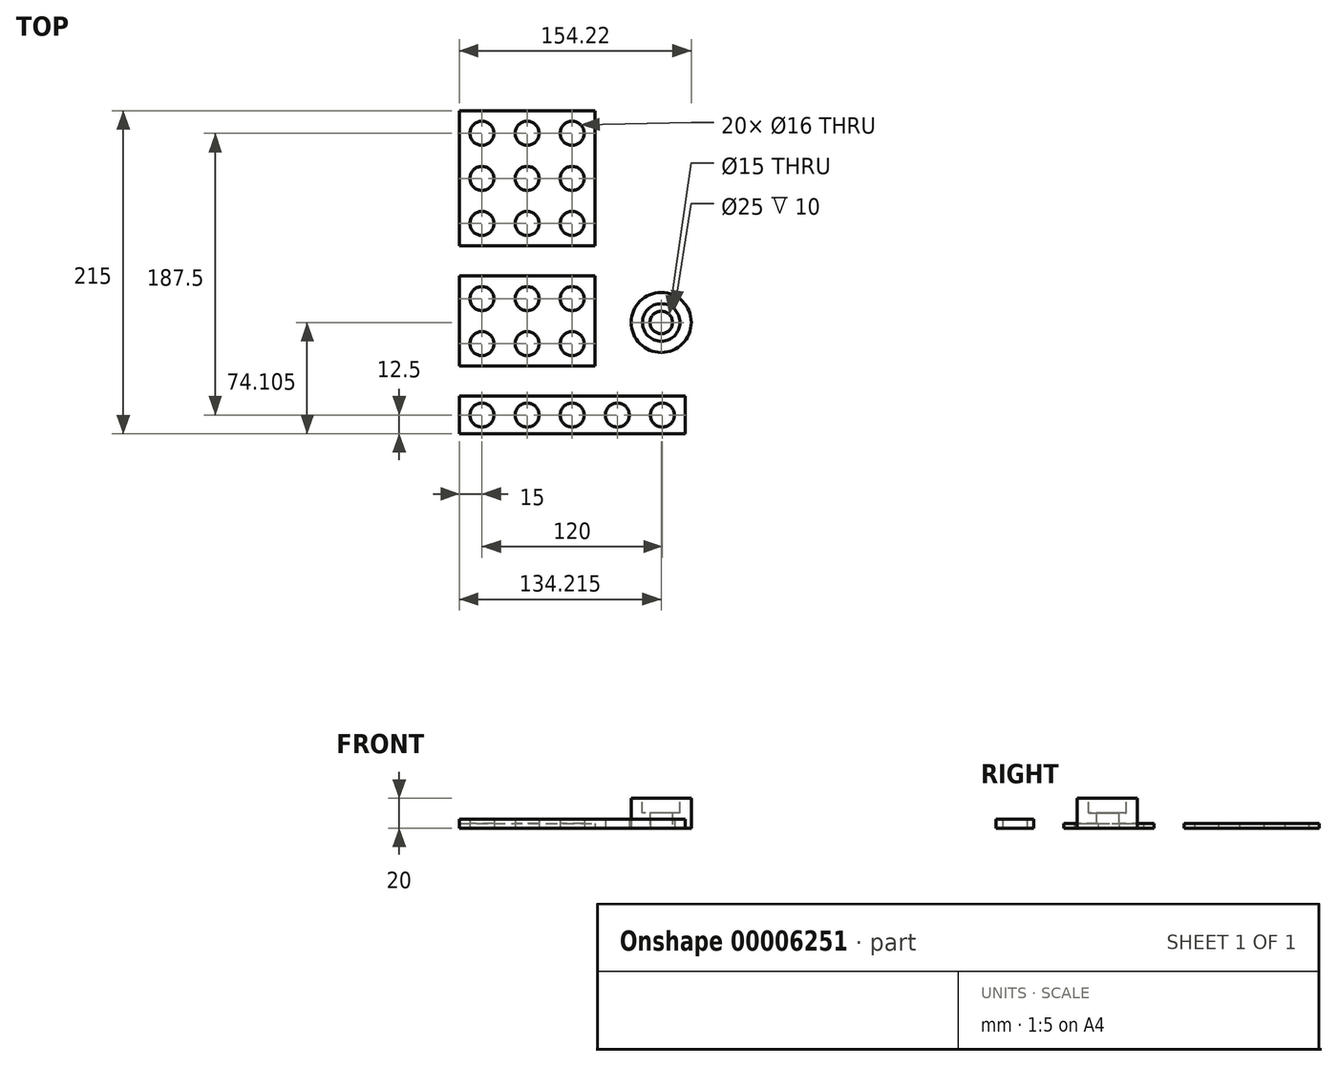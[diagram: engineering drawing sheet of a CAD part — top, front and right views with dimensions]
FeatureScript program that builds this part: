
annotation { "Feature Type Name" : "Feature", "Feature Type Description" : "" }
export const myFeature = defineFeature(function(context is Context, id is Id, definition is map)
    precondition{}
    {
        {
            var Q0;
            Q0=qCreatedBy(makeId("Top.planeOp"),FACE);
            var sketch = newSketch(context, id + "F0", { "sketchPlane" : qUnion([Q0])});
            skCircle(sketch, "E0", {"center": v(0, 0) * mm, "radius": 8 * mm});
            skLineSegment(sketch, "E1.bottom", {"start": v(-15, 12.5) * mm, "end": v(135, 12.5) * mm});
            skLineSegment(sketch, "E1.top", {"start": v(-15, -12.5) * mm, "end": v(135, -12.5) * mm});
            skLineSegment(sketch, "E1.left", {"start": v(-15, 12.5) * mm, "end": v(-15, -12.5) * mm});
            skLineSegment(sketch, "E1.right", {"start": v(135, 12.5) * mm, "end": v(135, -12.5) * mm});
            skCircle(sketch, "E2.1.0.0", {"center": v(30, 0) * mm, "radius": 8 * mm});
            skCircle(sketch, "E2.2.0.0", {"center": v(60, 0) * mm, "radius": 8 * mm});
            skCircle(sketch, "E2.3.0.0", {"center": v(90, 0) * mm, "radius": 8 * mm});
            skCircle(sketch, "E2.4.0.0", {"center": v(120, 0) * mm, "radius": 8 * mm});
            skLineSegment(sketch, "E2.direction1", {"start": v(0, 0) * mm, "end": v(30, 0) * mm, "construction": true});
            skLineSegment(sketch, "E3.bottom", {"start": v(-15, 32.5) * mm, "end": v(75, 32.5) * mm});
            skLineSegment(sketch, "E3.top", {"start": v(-15, 92.5) * mm, "end": v(75, 92.5) * mm});
            skLineSegment(sketch, "E3.left", {"start": v(-15, 32.5) * mm, "end": v(-15, 92.5) * mm});
            skLineSegment(sketch, "E3.right", {"start": v(75, 32.5) * mm, "end": v(75, 92.5) * mm});
            skCircle(sketch, "E4", {"center": v(0, 47.5) * mm, "radius": 8 * mm});
            skCircle(sketch, "E5.0.1.0", {"center": v(0, 77.5) * mm, "radius": 8 * mm});
            skCircle(sketch, "E5.1.0.0", {"center": v(30, 47.5) * mm, "radius": 8 * mm});
            skCircle(sketch, "E5.1.1.0", {"center": v(30, 77.5) * mm, "radius": 8 * mm});
            skCircle(sketch, "E5.2.0.0", {"center": v(60, 47.5) * mm, "radius": 8 * mm});
            skCircle(sketch, "E5.2.1.0", {"center": v(60, 77.5) * mm, "radius": 8 * mm});
            skLineSegment(sketch, "E5.direction1", {"start": v(0, 47.5) * mm, "end": v(30, 47.5) * mm, "construction": true});
            skLineSegment(sketch, "E5.direction2", {"start": v(0, 47.5) * mm, "end": v(0, 77.5) * mm, "construction": true});
            skLineSegment(sketch, "E6", {"start": v(30, 92.5) * mm, "end": v(30, 32.5) * mm, "construction": true});
            skPoint(sketch, "E7", {"position": v(30, 62.5) * mm});
            skLineSegment(sketch, "E8", {"start": v(30, 77.5) * mm, "end": v(30, 47.5) * mm, "construction": true});
            skLineSegment(sketch, "E9", {"start": v(60, 12.5) * mm, "end": v(60, -12.5) * mm, "construction": true});
            skLineSegment(sketch, "E10.bottom", {"start": v(-15, 112.5) * mm, "end": v(75, 112.5) * mm});
            skLineSegment(sketch, "E10.top", {"start": v(-15, 202.5) * mm, "end": v(75, 202.5) * mm});
            skLineSegment(sketch, "E10.left", {"start": v(-15, 112.5) * mm, "end": v(-15, 202.5) * mm});
            skLineSegment(sketch, "E10.right", {"start": v(75, 112.5) * mm, "end": v(75, 202.5) * mm});
            skCircle(sketch, "E11", {"center": v(0, 127.5) * mm, "radius": 8 * mm});
            skCircle(sketch, "E12.0.1.0", {"center": v(0, 157.5) * mm, "radius": 8 * mm});
            skCircle(sketch, "E12.0.2.0", {"center": v(0, 187.5) * mm, "radius": 8 * mm});
            skCircle(sketch, "E12.1.0.0", {"center": v(30, 127.5) * mm, "radius": 8 * mm});
            skCircle(sketch, "E12.1.1.0", {"center": v(30, 157.5) * mm, "radius": 8 * mm});
            skCircle(sketch, "E12.1.2.0", {"center": v(30, 187.5) * mm, "radius": 8 * mm});
            skCircle(sketch, "E12.2.0.0", {"center": v(60, 127.5) * mm, "radius": 8 * mm});
            skCircle(sketch, "E12.2.1.0", {"center": v(60, 157.5) * mm, "radius": 8 * mm});
            skCircle(sketch, "E12.2.2.0", {"center": v(60, 187.5) * mm, "radius": 8 * mm});
            skLineSegment(sketch, "E12.direction1", {"start": v(0, 127.5) * mm, "end": v(30, 127.5) * mm, "construction": true});
            skLineSegment(sketch, "E12.direction2", {"start": v(0, 127.5) * mm, "end": v(0, 157.5) * mm, "construction": true});
            skLineSegment(sketch, "E13", {"start": v(30, 202.5) * mm, "end": v(30, 112.5) * mm, "construction": true});
            skSolve(sketch);
        }
        {
            var Q0;
            Q0=makeQuery(id+"F0.imprint","IMPRINT",FACE,{"disambiguationData":[TD([[makeQuery(id+"F0.imprint","IMPRINT",EDGE,{"derivedFrom":sQuery(id+"F0.wireOp",EDGE,"E0")}),-1.0]])]});
            extrude(context, id + "F1", {"entities" : qUnion([Q0]), "depth" : 6 * mm});
        }
        {
            var Q0;
            Q0=makeQuery(id+"F0.imprint","IMPRINT",FACE,{"disambiguationData":[TD([[makeQuery(id+"F0.imprint","IMPRINT",EDGE,{"derivedFrom":sQuery(id+"F0.wireOp",EDGE,"E3.bottom")}),1.0]])]});
            extrude(context, id + "F2", {"entities" : qUnion([Q0]), "depth" : 3 * mm});
        }
        {
            var Q0;
            Q0=makeQuery(id+"F0.imprint","IMPRINT",FACE,{"disambiguationData":[TD([[makeQuery(id+"F0.imprint","IMPRINT",EDGE,{"derivedFrom":sQuery(id+"F0.wireOp",EDGE,"E10.bottom")}),1.0]])]});
            extrude(context, id + "F3", {"entities" : qUnion([Q0]), "depth" : 3 * mm});
        }
        {
            var Q0;
            Q0=qCreatedBy(makeId("Top.planeOp"),FACE);
            var sketch = newSketch(context, id + "F4", { "sketchPlane" : qUnion([Q0])});
            skCircle(sketch, "E14", {"center": v(119.22, 61.6) * mm, "radius": 7.5 * mm});
            skCircle(sketch, "E15", {"center": v(119.22, 61.6) * mm, "radius": 20 * mm});
            skSolve(sketch);
        }
        {
            var Q0;
            Q0=makeQuery(id+"F4.imprint","IMPRINT",FACE,{"disambiguationData":[TD([[makeQuery(id+"F4.imprint","IMPRINT",EDGE,{"derivedFrom":sQuery(id+"F4.wireOp",EDGE,"E14")}),-1.0]])]});
            extrude(context, id + "F5", {"entities" : qUnion([Q0]), "depth" : 20 * mm});
        }
        {
            var Q0;
            Q0=makeQuery(id+"F5.opExtrude","CAP_FACE",FACE,{"disambiguationData":[OSD([sQuery(id+"F4.wireOp",EDGE,"E14"),sQuery(id+"F4.wireOp",EDGE,"E15")])],"isStart":false});
            var sketch = newSketch(context, id + "F6", { "sketchPlane" : qUnion([Q0])});
            skCircle(sketch, "E16", {"center": v(119.22, 61.6) * mm, "radius": 12.5 * mm});
            skSolve(sketch);
        }
        {
            var Q0;
            Q0=makeQuery(id+"F6.imprint","IMPRINT",FACE,{"disambiguationData":[TD([[makeQuery(id+"F6.imprint","IMPRINT",EDGE,{"derivedFrom":sQuery(id+"F6.wireOp",EDGE,"E16")}),1.0]])]});
            extrude(context, id + "F7", {"entities" : qUnion([Q0]), "operationType" : NewBodyOperationType.REMOVE, "oppositeDirection" : true, "depth" : 10 * mm});
        }
    });
